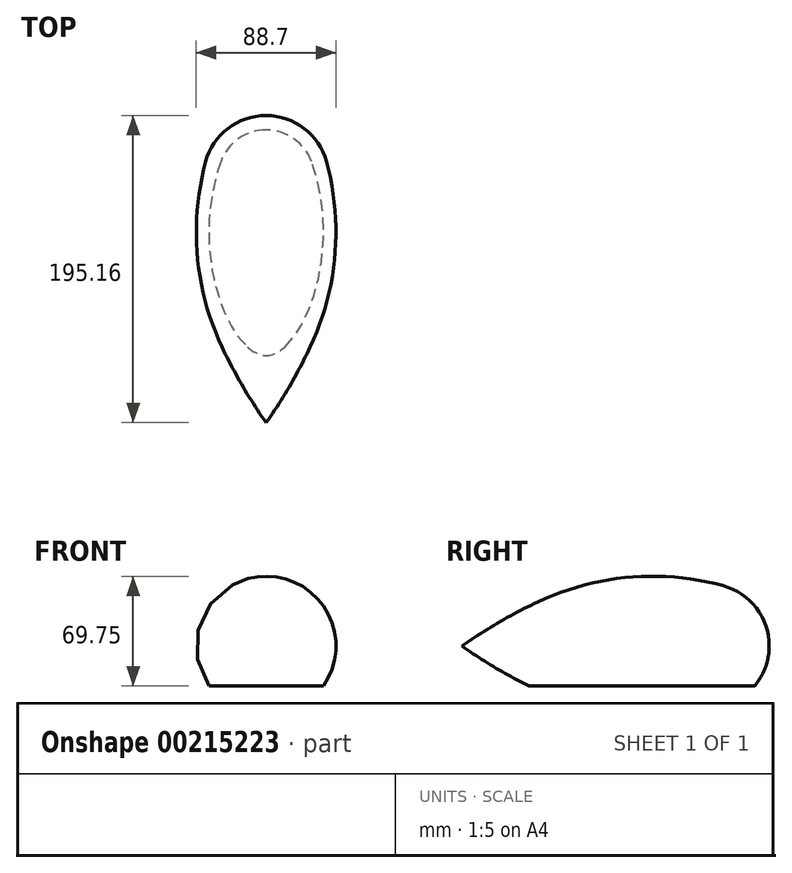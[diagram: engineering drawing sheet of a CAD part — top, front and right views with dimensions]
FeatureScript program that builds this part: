
annotation { "Feature Type Name" : "Feature", "Feature Type Description" : "" }
export const myFeature = defineFeature(function(context is Context, id is Id, definition is map)
    precondition{}
    {
        {
            var Q0;
            Q0=qCreatedBy(makeId("Right.planeOp"),FACE);
            var sketch = newSketch(context, id + "F0", { "sketchPlane" : qUnion([Q0])});
            skArc(sketch, "E0", {"start": v(0, 0) * mm, "mid": v(-8.18, 24.15) * mm, "end": v(-29.34, 38.37) * mm});
            skArc(sketch, "E1", {"start": v(-29.34, 38.37) * mm, "mid": v(-89.08, 43.7) * mm, "end": v(-146.97, 28.03) * mm});
            skArc(sketch, "E2", {"start": v(-146.97, 28.03) * mm, "mid": v(-171.67, 15.06) * mm, "end": v(-195.16, 0) * mm});
            skLineSegment(sketch, "E3", {"start": v(-195.16, 0) * mm, "end": v(0, 0) * mm});
            skSolve(sketch);
        }
        {
            var Q0;
            Q0=makeQuery(id+"F0.imprint","IMPRINT",FACE,{"disambiguationData":[TD([[makeQuery(id+"F0.imprint","IMPRINT",EDGE,{"derivedFrom":sQuery(id+"F0.wireOp",EDGE,"E0")}),1.0]])]});
            var Q1;
            Q1=sQuery(id+"F0.wireOp",EDGE,"E3");
            revolve(context, id + "F1", {"entities" : qUnion([Q0]), "axis" : qUnion([Q1]), "revolveType" : RevolveType.FULL});
        }
        {
            var Q0;
            Q0=qCreatedBy(makeId("Top.planeOp"),FACE);
            cPlane(context, id + "F2", {"entities" : qUnion([Q0]), "cplaneType" : CPlaneType.OFFSET, "offset" : 25.4 * mm, "oppositeDirection" : true, "width" : 152.4 * mm, "height" : 152.4 * mm});
        }
        {
            var Q0;
            Q0=qCreatedBy(id+"F2.planeOp",FACE);
            var sketch = newSketch(context, id + "F3", { "sketchPlane" : qUnion([Q0])});
            skCircle(sketch, "E4", {"center": v(0, -91.17) * mm, "radius": 146.28 * mm});
            skSolve(sketch);
        }
        {
            var Q0;
            Q0 = qSketchRegion(id + "F3", true);
            extrude(context, id + "F4", {"entities" : qUnion([Q0]), "operationType" : NewBodyOperationType.REMOVE, "oppositeDirection" : true, "depth" : 25.4 * mm});
        }
    });
